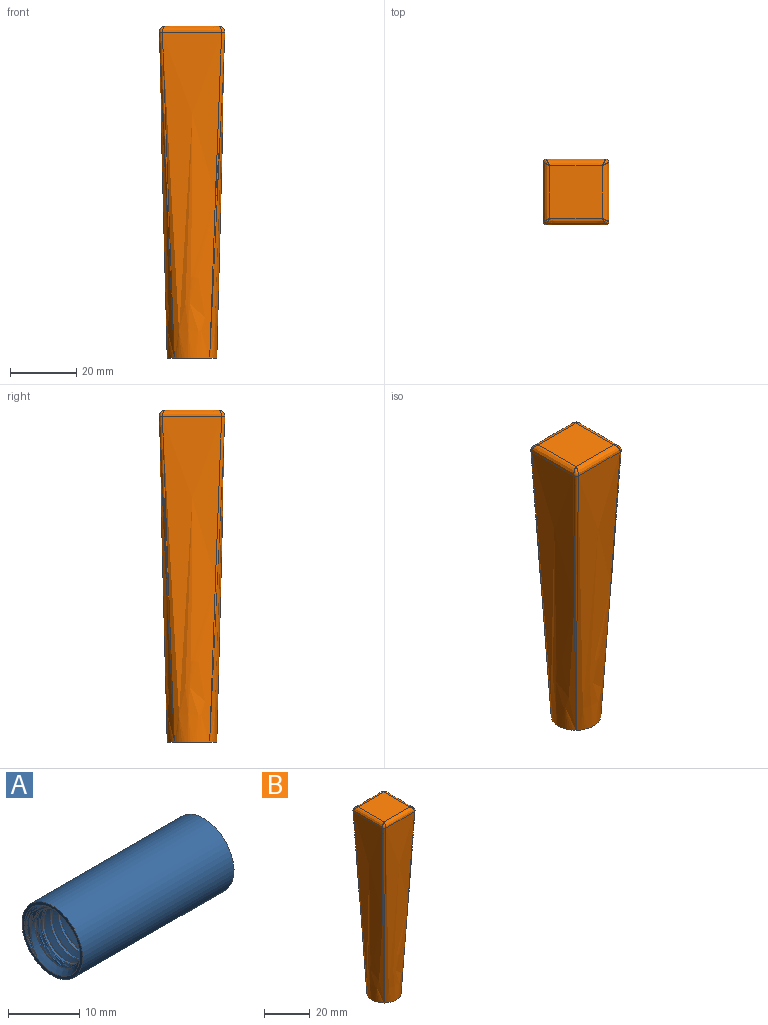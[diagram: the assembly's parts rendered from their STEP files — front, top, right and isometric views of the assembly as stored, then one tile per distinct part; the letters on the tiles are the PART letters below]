
ASSEMBLY  parts=2 mates=1
PART A: 8 faces, bbox 31.7x13x12.5 mm
  f0: cylinder r=4.47mm len=29mm, axis (1,0,0), area 224.8mm2, adj f3,f5,f6,f7
  f1: cylinder r=6mm len=30mm, axis (1,0,0), area 1131mm2, adj f2,f3
  f2: plane 12x12mm, normal (-1,0,0), area 18.9mm2, adj f1,f7
  f3: plane 12.46x12.46mm, normal (1,0,0), area 38.7mm2, adj f0,f1,f4,f5,f6
  f4: bspline ~30.63x12.52mm, area 151.6mm2, adj f3,f5,f6,f7
  f5: bspline ~31.19x12.32mm, area 567mm2, adj f0,f3,f4,f7
  f6: bspline ~30.66x12.32mm, area 566.5mm2, adj f0,f3,f4,f7
  f7: cone r=5.47mm half-angle=45deg, axis (-1,0,0), area 27.9mm2, adj f0,f2,f4,f5,f6
PART B: 20 faces, bbox 28.7x28.7x104.1 mm
  f0: plane 15x15mm, normal (0,0,-1), area 63.6mm2, adj f2,f3,f4,f5,f18
  f1: plane 15.9x15.9mm, normal (0,0,1), area 252.1mm2, adj f6,f7,f8,f9
  f2: bspline ~100x20mm, area 1443mm2, adj f0,f8,f14,f16
  f3: bspline ~100x20mm, area 1443mm2, adj f0,f6,f12,f14
  f4: bspline ~100x20mm, area 1443mm2, adj f0,f7,f10,f12
  f5: bspline ~100x20mm, area 1443mm2, adj f0,f9,f10,f16
  f6: bspline ~26.88x2.14mm, area 53.9mm2, adj f1,f3,f13,f15
  f7: bspline ~26.88x2.14mm, area 53.9mm2, adj f1,f4,f11,f13
  f8: bspline ~26.88x2.14mm, area 53.9mm2, adj f1,f2,f15,f17
  f9: bspline ~26.88x2.14mm, area 53.9mm2, adj f1,f5,f11,f17
  f10: bspline ~104.07x4.88mm, area 58.9mm2, adj f4,f5,f11
  f11: bspline ~2.53x1.99mm, area 2.4mm2, adj f7,f9,f10
  f12: bspline ~104.07x4.88mm, area 58.9mm2, adj f3,f4,f13
  f13: bspline ~2.53x1.99mm, area 2.4mm2, adj f6,f7,f12
  f14: bspline ~104.07x4.88mm, area 58.9mm2, adj f2,f3,f15
  f15: bspline ~2.53x1.99mm, area 2.4mm2, adj f6,f8,f14
  f16: bspline ~104.07x4.88mm, area 58.9mm2, adj f2,f5,f17
  f17: bspline ~2.53x1.99mm, area 2.4mm2, adj f8,f9,f16
  f18: cylinder r=6mm len=30mm, axis (0,0,-1), area 1131mm2, adj f0,f19
  f19: plane 12x12mm, normal (0,0,-1), area 113.1mm2, adj f18
PLACE A rot(axis=(0,-1,0),90deg) t=(0.75,21.31,-11.59)mm
PLACE B t=(0.75,21.31,-41.59)mm
MATE fastened A.f1 <-> B.f18  axis (0,0,1) through (0.75,21.31,-11.59)mm
